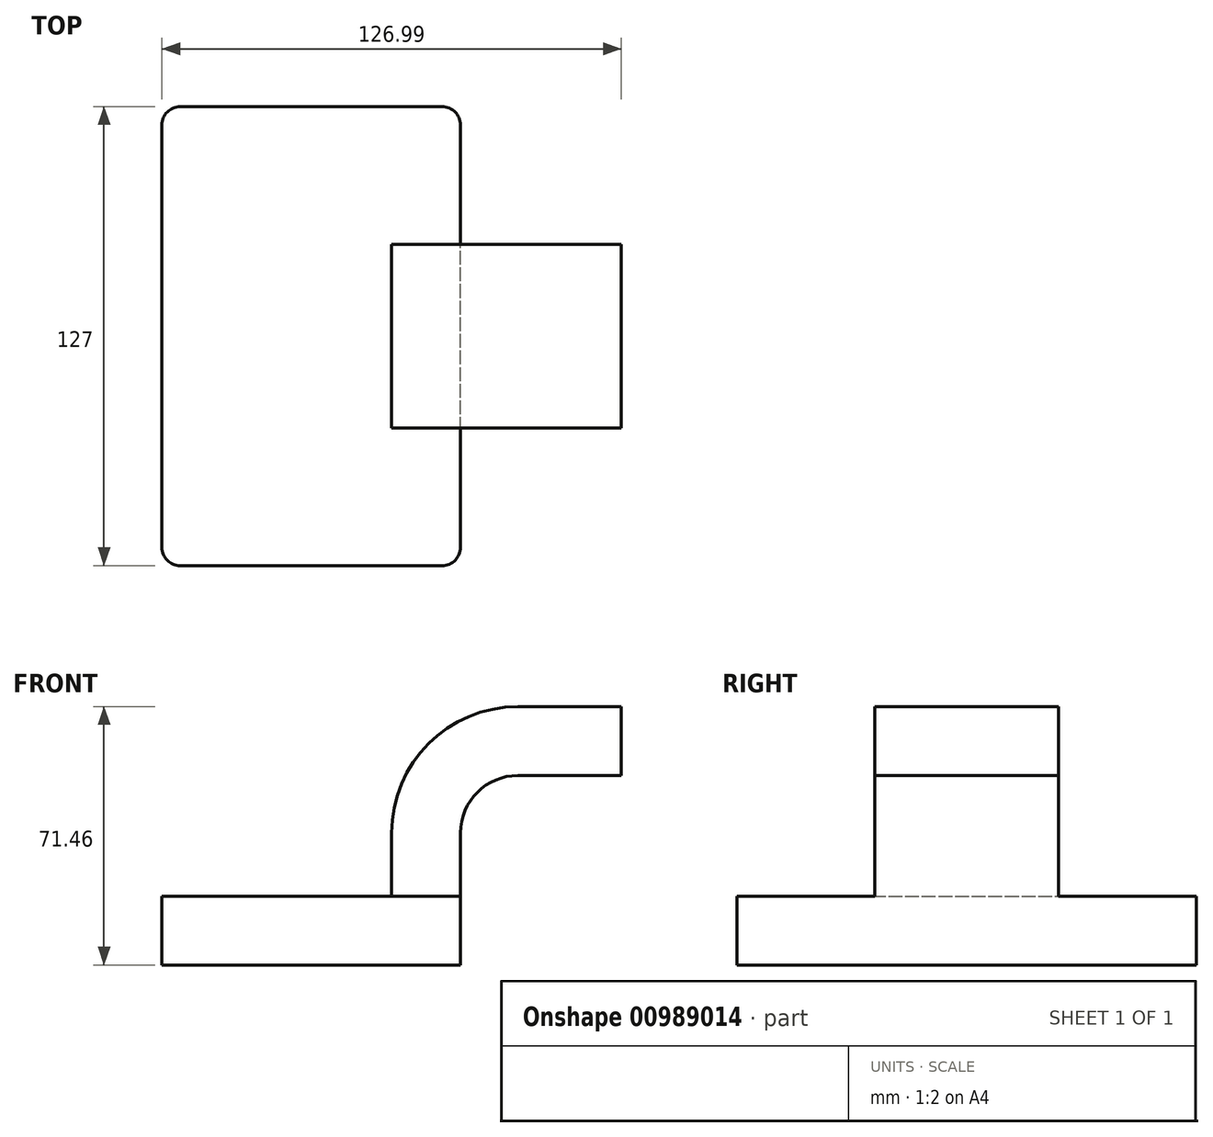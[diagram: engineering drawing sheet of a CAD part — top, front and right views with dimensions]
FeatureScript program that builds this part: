
annotation { "Feature Type Name" : "Feature", "Feature Type Description" : "" }
export const myFeature = defineFeature(function(context is Context, id is Id, definition is map)
    precondition{}
    {
        {
            var Q0;
            Q0=qCreatedBy(makeId("Front.planeOp"),FACE);
            var sketch = newSketch(context, id + "F0", { "sketchPlane" : qUnion([Q0])});
            skLineSegment(sketch, "E0.bottom", {"start": v(-41.28, 9.52) * mm, "end": v(41.28, 9.53) * mm});
            skLineSegment(sketch, "E0.top", {"start": v(-41.28, -9.53) * mm, "end": v(41.28, -9.53) * mm});
            skLineSegment(sketch, "E0.left", {"start": v(-41.28, 9.52) * mm, "end": v(-41.28, -9.53) * mm});
            skLineSegment(sketch, "E0.right", {"start": v(41.28, 9.53) * mm, "end": v(41.28, -9.52) * mm});
            skPoint(sketch, "E0.middle", {"position": v(0, 0) * mm});
            skLineSegment(sketch, "E1", {"start": v(41.27, 9.53) * mm, "end": v(41.27, 27) * mm});
            skLineSegment(sketch, "E2.bottom", {"start": v(60.33, 38.1) * mm, "end": v(111.12, 38.1) * mm});
            skLineSegment(sketch, "E2.top", {"start": v(60.33, 66.67) * mm, "end": v(111.12, 66.67) * mm});
            skLineSegment(sketch, "E2.left", {"start": v(60.33, 38.1) * mm, "end": v(60.32, 66.67) * mm});
            skLineSegment(sketch, "E2.right", {"start": v(111.12, 38.1) * mm, "end": v(111.12, 66.67) * mm});
            skPoint(sketch, "E2.middle", {"position": v(85.72, 52.39) * mm});
            skArc(sketch, "E3", {"start": v(41.27, 27) * mm, "mid": v(45.92, 38.23) * mm, "end": v(57.15, 42.88) * mm});
            skLineSegment(sketch, "E4", {"start": v(57.15, 42.88) * mm, "end": v(85.72, 42.88) * mm});
            skLineSegment(sketch, "E5.0", {"start": v(57.15, 61.93) * mm, "end": v(85.72, 61.93) * mm});
            skArc(sketch, "E5.1", {"start": v(22.23, 27) * mm, "mid": v(32.45, 51.7) * mm, "end": v(57.15, 61.93) * mm});
            skLineSegment(sketch, "E5.2", {"start": v(22.22, 9.53) * mm, "end": v(22.22, 27) * mm});
            skLineSegment(sketch, "E6", {"start": v(85.72, 38.1) * mm, "end": v(85.72, 66.67) * mm});
            skFitSpline(sketch, "E7", {"points": [v(-41.28, 9.52) * mm, v(57.15, 61.93) * mm], "startDerivative": vector(68.73, 65.22) * mm, "endDerivative": vector(130.65, -5.6) * mm});
            skSolve(sketch);
        }
        {
            var Q0;
            Q0=makeQuery(id+"F0.imprint","IMPRINT",FACE,{"disambiguationData":[TD([[makeQuery(id+"F0.imprint","IMPRINT",EDGE,{"derivedFrom":sQuery(id+"F0.wireOp",EDGE,"E0.top")}),1.0]])]});
            extrude(context, id + "F1", {"entities" : qUnion([Q0]), "endBound" : BoundingType.SYMMETRIC, "depth" : 127 * mm, "offsetDistance" : 25.4 * mm});
        }
        {
            var Q0;
            {var subQ1=sQuery(id+"F0.wireOp",EDGE,"E1");Q0=makeQuery(id+"F0.imprint","IMPRINT",FACE,{"disambiguationData":[TD([[makeQuery(id+"F0.imprint","IMPRINT",EDGE,{"derivedFrom":subQ1}),1.0]])]});}
            var Q1;
            {var subQ0=sQuery(id+"F0.wireOp",EDGE,"E4");var subQ1=sQuery(id+"F0.wireOp",EDGE,"E2.left");var subQ2=makeQuery(id+"F0.imprint","INTERSECT",VERTEX,{"derivedFrom":[subQ1,subQ0]});Q1=makeQuery(id+"F0.imprint","IMPRINT",FACE,{"disambiguationData":[TD([[makeQuery(id+"F0.imprint","IMPRINT",EDGE,{"disambiguationData":[TD([[subQ2,-1.0]])],"derivedFrom":subQ1}),-1.0]])]});}
            extrude(context, id + "F2", {"entities" : qUnion([Q0, Q1]), "operationType" : NewBodyOperationType.ADD, "endBound" : BoundingType.SYMMETRIC, "depth" : 50.8 * mm, "offsetDistance" : 25.4 * mm});
        }
        {
            var Q0;
            Q0=makeQuery(id+"F0.imprint","IMPRINT",FACE,{"disambiguationData":[TD([[makeQuery(id+"F0.imprint","IMPRINT",EDGE,{"derivedFrom":sQuery(id+"F0.wireOp",EDGE,"E5.1")}),1.0]])]});
            extrude(context, id + "F3", {"entities" : qUnion([Q0]), "operationType" : NewBodyOperationType.ADD, "endBound" : BoundingType.SYMMETRIC, "depth" : 15.88 * mm, "offsetDistance" : 25.4 * mm});
        }
        {
            var Q0;
            Q0=makeQuery(id+"F1.opExtrude","CAP_EDGE",EDGE,{"disambiguationData":[OSD([sQuery(id+"F0.wireOp",EDGE,"E0.right")])],"isStart":false});
            var Q1;
            Q1=makeQuery(id+"F1.opExtrude","CAP_EDGE",EDGE,{"disambiguationData":[OSD([sQuery(id+"F0.wireOp",EDGE,"E0.left")])],"isStart":false});
            var Q2;
            Q2=makeQuery(id+"F1.opExtrude","CAP_EDGE",EDGE,{"disambiguationData":[OSD([sQuery(id+"F0.wireOp",EDGE,"E0.right")])],"isStart":true});
            var Q3;
            Q3=makeQuery(id+"F1.opExtrude","CAP_EDGE",EDGE,{"disambiguationData":[OSD([sQuery(id+"F0.wireOp",EDGE,"E0.left")])],"isStart":true});
            fillet(context, id + "F4", {"entities" : qUnion([Q0, Q1, Q2, Q3]), "radius" : 5.08 * mm, "tangentPropagation" : true, "allowEdgeOverflow" : false});
        }
    });
